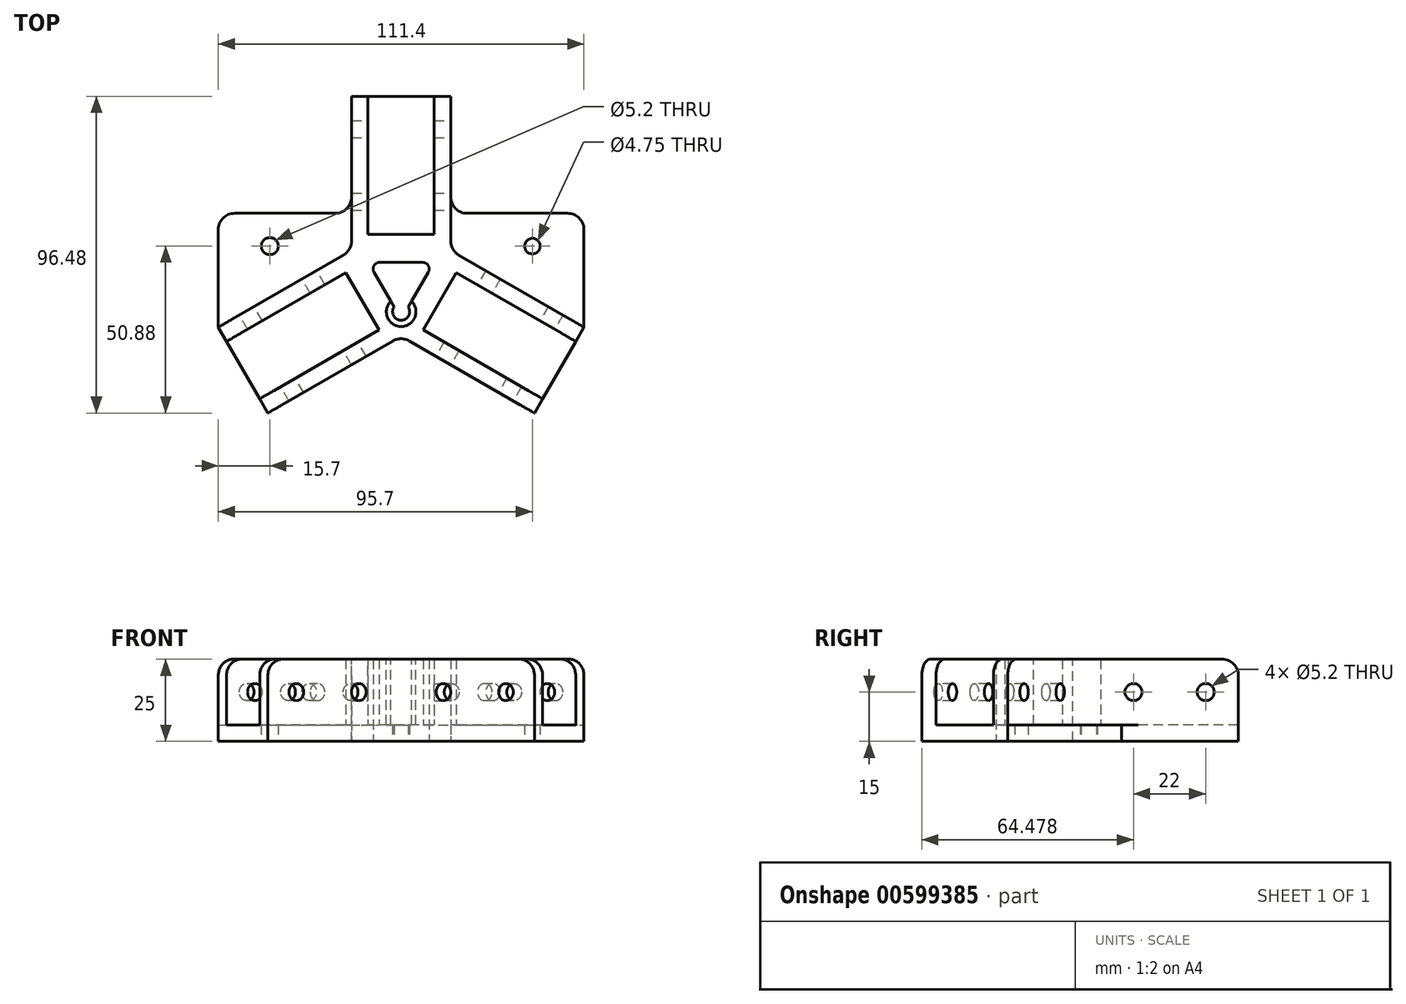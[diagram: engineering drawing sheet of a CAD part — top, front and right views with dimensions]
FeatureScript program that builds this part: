
annotation { "Feature Type Name" : "Feature", "Feature Type Description" : "" }
export const myFeature = defineFeature(function(context is Context, id is Id, definition is map)
    precondition{}
    {
        {
            var Q0;
            Q0=qCreatedBy(makeId("Top.planeOp"),FACE);
            var sketch = newSketch(context, id + "F0", { "sketchPlane" : qUnion([Q0])});
            skLineSegment(sketch, "E0", {"start": v(0, 0) * mm, "end": v(140.3, -81) * mm, "construction": true});
            skLineSegment(sketch, "E1", {"start": v(0, 0) * mm, "end": v(0, 45.49) * mm, "construction": true});
            skLineSegment(sketch, "E2", {"start": v(6.73, -15.55) * mm, "end": v(43.1, -36.55) * mm});
            skLineSegment(sketch, "E3", {"start": v(40.6, -40.88) * mm, "end": v(43.1, -36.55) * mm});
            skLineSegment(sketch, "E4", {"start": v(53.2, -19.05) * mm, "end": v(16.83, 1.95) * mm});
            skLineSegment(sketch, "E5", {"start": v(-0.2, -17.32) * mm, "end": v(40.6, -40.88) * mm});
            skLineSegment(sketch, "E6", {"start": v(55.7, -14.72) * mm, "end": v(14.9, 8.83) * mm});
            skLineSegment(sketch, "E7.trimOffspring", {"start": v(53.2, -19.05) * mm, "end": v(55.7, -14.72) * mm});
            skPoint(sketch, "E8.startSnap0", {"position": v(7.5, -4.33) * mm});
            skPoint(sketch, "E9.orphan", {"position": v(0, -11.66) * mm});
            skLineSegment(sketch, "E10", {"start": v(6.73, -15.55) * mm, "end": v(16.83, 1.95) * mm});
            skLineSegment(sketch, "E11", {"start": v(14.9, 8.83) * mm, "end": v(0, 0) * mm});
            skLineSegment(sketch, "E12", {"start": v(0, 0) * mm, "end": v(-0.2, -17.32) * mm});
            skPoint(sketch, "E13.endSnap0", {"position": v(11.78, -6.8) * mm});
            skLineSegment(sketch, "E14", {"start": v(16.86, 1.81) * mm, "end": v(6.86, -15.5) * mm, "construction": true});
            skLineSegment(sketch, "E15", {"start": v(6.86, -15.5) * mm, "end": v(147.16, -96.5) * mm, "construction": true});
            skLineSegment(sketch, "E16", {"start": v(157.16, -79.19) * mm, "end": v(16.86, 1.81) * mm, "construction": true});
            skLineSegment(sketch, "E17.bottom", {"start": v(-152.4, 152.4) * mm, "end": v(152.4, 152.4) * mm, "construction": true});
            skLineSegment(sketch, "E17.top", {"start": v(-152.4, -152.4) * mm, "end": v(152.4, -152.4) * mm, "construction": true});
            skLineSegment(sketch, "E17.left", {"start": v(-152.4, 152.4) * mm, "end": v(-152.4, -152.4) * mm, "construction": true});
            skLineSegment(sketch, "E17.right", {"start": v(152.4, 152.4) * mm, "end": v(152.4, -152.4) * mm, "construction": true});
            skLineSegment(sketch, "E18.bottom", {"start": v(-250, 230) * mm, "end": v(250, 230) * mm, "construction": true});
            skLineSegment(sketch, "E18.top", {"start": v(-250, -230) * mm, "end": v(250, -230) * mm, "construction": true});
            skLineSegment(sketch, "E18.left", {"start": v(-250, 230) * mm, "end": v(-250, -230) * mm, "construction": true});
            skLineSegment(sketch, "E19.top", {"start": v(-250, 250) * mm, "end": v(250, 250) * mm, "construction": true});
            skLineSegment(sketch, "E19.left", {"start": v(-250, 230) * mm, "end": v(-250, 250) * mm, "construction": true});
            skLineSegment(sketch, "E19.right", {"start": v(250, 230) * mm, "end": v(250, 250) * mm, "construction": true});
            skLineSegment(sketch, "E20.bottom", {"start": v(-250, 250) * mm, "end": v(-270, 250) * mm, "construction": true});
            skLineSegment(sketch, "E20.top", {"start": v(-250, -250) * mm, "end": v(-270, -250) * mm, "construction": true});
            skLineSegment(sketch, "E20.left", {"start": v(-250, 250) * mm, "end": v(-250, -250) * mm, "construction": true});
            skLineSegment(sketch, "E20.right", {"start": v(-270, 250) * mm, "end": v(-270, -250) * mm, "construction": true});
            skLineSegment(sketch, "E21.bottom", {"start": v(250, 250) * mm, "end": v(270, 250) * mm, "construction": true});
            skLineSegment(sketch, "E21.top", {"start": v(250, -250) * mm, "end": v(270, -250) * mm, "construction": true});
            skLineSegment(sketch, "E21.left", {"start": v(250, 250) * mm, "end": v(250, -117.97) * mm, "construction": true});
            skLineSegment(sketch, "E21.right", {"start": v(270, 250) * mm, "end": v(270, -250) * mm, "construction": true});
            skLineSegment(sketch, "E22.bottom", {"start": v(-250, -250) * mm, "end": v(250, -250) * mm, "construction": true});
            skLineSegment(sketch, "E22.left", {"start": v(-250, -250) * mm, "end": v(-250, -230) * mm, "construction": true});
            skLineSegment(sketch, "E22.right", {"start": v(250, -250) * mm, "end": v(250, -230) * mm, "construction": true});
            skLineSegment(sketch, "E23", {"start": v(260, -238.46) * mm, "end": v(260, 217.54) * mm, "construction": true});
            skLineSegment(sketch, "E24.trimOffspring", {"start": v(250, -117.97) * mm, "end": v(250, -250) * mm, "construction": true});
            skPoint(sketch, "E25", {"position": v(152.4, -87.99) * mm});
            skLineSegment(sketch, "E26", {"start": v(147.16, -96.5) * mm, "end": v(157.16, -79.19) * mm, "construction": true});
            skCircle(sketch, "E27", {"center": v(147.4, -85.1) * mm, "radius": 2.65 * mm, "construction": true});
            skSolve(sketch);
        }
        {
            var Q0;
            Q0=qSketchRegion(id+"F0",true);
            extrude(context, id + "F1", {"entities" : qUnion([Q0]), "depth" : 20 * mm});
        }
        {
            var Q0;
            Q0=makeQuery(id+"F8AnNkQhTy7cih4_3.boolean.opBoolean","MERGE",FACE,{"derivedFrom":[makeQuery(id+"F1.opExtrude","SWEPT_FACE",FACE,{"disambiguationData":[OSD([sQuery(id+"F0.wireOp",EDGE,"E5")])]}),makeQuery(id+"F8AnNkQhTy7cih4_3.opExtrude","SWEPT_FACE",FACE,{"disambiguationData":[OSD([sQuery(id+"FXKs39bWKYu9lIt_3.wireOp",EDGE,"d46a372c-ea87-446f-ae03-e79ca4958cda.0")])]})]});
            var sketch = newSketch(context, id + "F2", { "sketchPlane" : qUnion([Q0])});
            skCircle(sketch, "E28", {"center": v(45.6, 10) * mm, "radius": 2.6 * mm});
            skCircle(sketch, "E29", {"center": v(23.6, 10) * mm, "radius": 2.6 * mm});
            skSolve(sketch);
        }
        {
            var Q0;
            Q0=qSketchRegion(id+"F2",true);
            extrude(context, id + "F3", {"entities" : qUnion([Q0]), "operationType" : NewBodyOperationType.REMOVE, "endBound" : BoundingType.THROUGH_ALL, "oppositeDirection" : true, "depth" : 25 * mm});
        }
        {
            var Q0;
            Q0=makeQuery(id+"F1.opExtrude","SWEPT_BODY",BODY,{"disambiguationData":[OSD([sQuery(id+"F0.wireOp",EDGE,"E2"),sQuery(id+"F0.wireOp",EDGE,"E3"),sQuery(id+"F0.wireOp",EDGE,"E4"),sQuery(id+"F0.wireOp",EDGE,"E5"),sQuery(id+"F0.wireOp",EDGE,"E6"),sQuery(id+"F0.wireOp",EDGE,"E7.trimOffspring"),sQuery(id+"F0.wireOp",EDGE,"E10"),sQuery(id+"F0.wireOp",EDGE,"E11"),sQuery(id+"F0.wireOp",EDGE,"E12")])]});
            var Q1;
            Q1=makeQuery(id+"F1.opExtrude","SWEPT_EDGE",EDGE,{"disambiguationData":[OSD([sQuery(id+"F0.wireOp",EDGE,"E11"),sQuery(id+"F0.wireOp",EDGE,"E12")])]});
            circularPattern(context, id + "F4", {"operationType" : NewBodyOperationType.ADD, "entities" : qUnion([Q0]), "axis" : qUnion([Q1]), "angle" : 120 * degree, "instanceCount" : round(3)});
        }
        {
            var Q0;
            {var subQ0=makeQuery(id+"F1.opExtrude","CAP_FACE",FACE,{"disambiguationData":[OSD([sQuery(id+"F0.wireOp",EDGE,"E2"),sQuery(id+"F0.wireOp",EDGE,"E3"),sQuery(id+"F0.wireOp",EDGE,"E4"),sQuery(id+"F0.wireOp",EDGE,"E5"),sQuery(id+"F0.wireOp",EDGE,"E6"),sQuery(id+"F0.wireOp",EDGE,"E7.trimOffspring"),sQuery(id+"F0.wireOp",EDGE,"E10"),sQuery(id+"F0.wireOp",EDGE,"E11"),sQuery(id+"F0.wireOp",EDGE,"E12")])],"isStart":true});Q0=makeQuery(id+"F4.boolean.opBoolean","MERGE",FACE,{"derivedFrom":[subQ0,makeQuery(id+"F4.opPattern","COPY",FACE,{"derivedFrom":subQ0,"instanceName":"1"}),makeQuery(id+"F4.opPattern","COPY",FACE,{"derivedFrom":subQ0,"instanceName":"2"})]});}
            var sketch = newSketch(context, id + "F5", { "sketchPlane" : qUnion([Q0])});
            skLineSegment(sketch, "E30.0", {"start": v(-40.6, 40.88) * mm, "end": v(0, 17.44) * mm});
            skLineSegment(sketch, "E31.0", {"start": v(0, 17.44) * mm, "end": v(40.6, 40.88) * mm});
            skLineSegment(sketch, "E32.0", {"start": v(55.7, 14.72) * mm, "end": v(15.1, -8.72) * mm});
            skLineSegment(sketch, "E33.0", {"start": v(15.1, -8.72) * mm, "end": v(15.1, -55.6) * mm});
            skLineSegment(sketch, "E34.0", {"start": v(-15.1, -55.6) * mm, "end": v(-15.1, -8.72) * mm});
            skLineSegment(sketch, "E35.0", {"start": v(-15.1, -8.72) * mm, "end": v(-55.7, 14.72) * mm});
            skLineSegment(sketch, "E36", {"start": v(-40.6, 40.88) * mm, "end": v(-55.7, 14.72) * mm});
            skLineSegment(sketch, "E37", {"start": v(40.6, 40.88) * mm, "end": v(55.7, 14.72) * mm});
            skLineSegment(sketch, "E38", {"start": v(15.1, -55.6) * mm, "end": v(-15.1, -55.6) * mm});
            skSolve(sketch);
        }
        {
            var Q0;
            Q0=qSketchRegion(id+"F5",true);
            extrude(context, id + "F6", {"entities" : qUnion([Q0]), "operationType" : NewBodyOperationType.ADD, "depth" : 5 * mm});
        }
        {
            var Q0;
            Q0=makeQuery(id+"F6.boolean.opBoolean","MERGE",EDGE,{"derivedFrom":[makeQuery(id+"F4.boolean.opBoolean","INTERSECT",EDGE,{"derivedFrom":[makeQuery(id+"F1.opExtrude","SWEPT_FACE",FACE,{"disambiguationData":[OSD([sQuery(id+"F0.wireOp",EDGE,"E5")])]}),makeQuery(id+"F4.opPattern","COPY",FACE,{"derivedFrom":makeQuery(id+"F1.opExtrude","SWEPT_FACE",FACE,{"disambiguationData":[OSD([sQuery(id+"F0.wireOp",EDGE,"E6")])]}),"instanceName":"1"})]}),makeQuery(id+"F6.opExtrude","SWEPT_EDGE",EDGE,{"disambiguationData":[OSD([sQuery(id+"F5.wireOp",EDGE,"E30.0"),sQuery(id+"F5.wireOp",EDGE,"E31.0")])]})]});
            var Q1;
            Q1=makeQuery(id+"F6.boolean.opBoolean","MERGE",EDGE,{"derivedFrom":[makeQuery(id+"F4.boolean.opBoolean","INTERSECT",EDGE,{"derivedFrom":[makeQuery(id+"F1.opExtrude","SWEPT_FACE",FACE,{"disambiguationData":[OSD([sQuery(id+"F0.wireOp",EDGE,"E6")])]}),makeQuery(id+"F4.opPattern","COPY",FACE,{"derivedFrom":makeQuery(id+"F1.opExtrude","SWEPT_FACE",FACE,{"disambiguationData":[OSD([sQuery(id+"F0.wireOp",EDGE,"E5")])]}),"instanceName":"2"})]}),makeQuery(id+"F6.opExtrude","SWEPT_EDGE",EDGE,{"disambiguationData":[OSD([sQuery(id+"F5.wireOp",EDGE,"E32.0"),sQuery(id+"F5.wireOp",EDGE,"E33.0")])]})]});
            var Q2;
            Q2=makeQuery(id+"F6.boolean.opBoolean","MERGE",EDGE,{"derivedFrom":[makeQuery(id+"F4.boolean.opBoolean","INTERSECT",EDGE,{"derivedFrom":[makeQuery(id+"F4.opPattern","COPY",FACE,{"derivedFrom":makeQuery(id+"F1.opExtrude","SWEPT_FACE",FACE,{"disambiguationData":[OSD([sQuery(id+"F0.wireOp",EDGE,"E5")])]}),"instanceName":"1"}),makeQuery(id+"F4.opPattern","COPY",FACE,{"derivedFrom":makeQuery(id+"F1.opExtrude","SWEPT_FACE",FACE,{"disambiguationData":[OSD([sQuery(id+"F0.wireOp",EDGE,"E6")])]}),"instanceName":"2"})]}),makeQuery(id+"F6.opExtrude","SWEPT_EDGE",EDGE,{"disambiguationData":[OSD([sQuery(id+"F5.wireOp",EDGE,"E34.0"),sQuery(id+"F5.wireOp",EDGE,"E35.0")])]})]});
            fillet(context, id + "F7", {"entities" : qUnion([Q0, Q1, Q2]), "radius" : 5 * mm, "tangentPropagation" : true, "allowEdgeOverflow" : false});
        }
        {
            var Q0;
            {var subQ0=makeQuery(id+"F1.opExtrude","CAP_FACE",FACE,{"disambiguationData":[OSD([sQuery(id+"F0.wireOp",EDGE,"E2"),sQuery(id+"F0.wireOp",EDGE,"E3"),sQuery(id+"F0.wireOp",EDGE,"E4"),sQuery(id+"F0.wireOp",EDGE,"E5"),sQuery(id+"F0.wireOp",EDGE,"E6"),sQuery(id+"F0.wireOp",EDGE,"E7.trimOffspring"),sQuery(id+"F0.wireOp",EDGE,"E10"),sQuery(id+"F0.wireOp",EDGE,"E11"),sQuery(id+"F0.wireOp",EDGE,"E12")])],"isStart":false});Q0=makeQuery(id+"F4.boolean.opBoolean","MERGE",FACE,{"derivedFrom":[subQ0,makeQuery(id+"F4.opPattern","COPY",FACE,{"derivedFrom":subQ0,"instanceName":"1"}),makeQuery(id+"F4.opPattern","COPY",FACE,{"derivedFrom":subQ0,"instanceName":"2"})]});}
            var sketch = newSketch(context, id + "F8", { "sketchPlane" : qUnion([Q0])});
            skLineSegment(sketch, "E39", {"start": v(-10, 5.06) * mm, "end": v(0, -12.26) * mm});
            skLineSegment(sketch, "E40", {"start": v(0, -12.26) * mm, "end": v(10, 5.06) * mm});
            skLineSegment(sketch, "E41", {"start": v(10, 5.06) * mm, "end": v(-10, 5.06) * mm});
            skSolve(sketch);
        }
        {
            var Q0;
            Q0=makeQuery(id+"F6.opExtrude","CAP_FACE",FACE,{"disambiguationData":[OSD([sQuery(id+"F5.wireOp",EDGE,"E30.0"),sQuery(id+"F5.wireOp",EDGE,"E31.0"),sQuery(id+"F5.wireOp",EDGE,"E32.0"),sQuery(id+"F5.wireOp",EDGE,"E33.0"),sQuery(id+"F5.wireOp",EDGE,"E34.0"),sQuery(id+"F5.wireOp",EDGE,"E35.0"),sQuery(id+"F5.wireOp",EDGE,"E36"),sQuery(id+"F5.wireOp",EDGE,"E37"),sQuery(id+"F5.wireOp",EDGE,"E38")])],"isStart":false});
            var sketch = newSketch(context, id + "F9", { "sketchPlane" : qUnion([Q0])});
            skLineSegment(sketch, "E42.top", {"start": v(-55.7, -20) * mm, "end": v(55.7, -20) * mm});
            skLineSegment(sketch, "E42.left", {"start": v(-55.7, 14.72) * mm, "end": v(-55.7, -20) * mm});
            skLineSegment(sketch, "E42.right", {"start": v(55.7, 14.72) * mm, "end": v(55.7, -20) * mm});
            skLineSegment(sketch, "E43", {"start": v(-52.65, 20) * mm, "end": v(-4.44, 20) * mm});
            skLineSegment(sketch, "E44", {"start": v(52.65, 20) * mm, "end": v(55.7, 14.72) * mm});
            skPoint(sketch, "E45.start.orphan", {"position": v(-52.65, 20) * mm});
            skLineSegment(sketch, "E46", {"start": v(-52.65, 20) * mm, "end": v(-55.7, 14.72) * mm});
            skPoint(sketch, "E47.orphan", {"position": v(-55.7, 20) * mm});
            skArc(sketch, "E48.0", {"start": v(2.5, 18.88) * mm, "mid": v(0, 18.2) * mm, "end": v(-2.5, 18.88) * mm});
            skLineSegment(sketch, "E48.1", {"start": v(2.5, 18.88) * mm, "end": v(4.44, 20) * mm});
            skLineSegment(sketch, "E48.2", {"start": v(-4.44, 20) * mm, "end": v(-2.5, 18.88) * mm});
            skPoint(sketch, "E49.orphan", {"position": v(-40.6, 40.88) * mm});
            skPoint(sketch, "E50.orphan", {"position": v(40.6, 40.88) * mm});
            skLineSegment(sketch, "E51.trimOffspring", {"start": v(4.44, 20) * mm, "end": v(52.65, 20) * mm});
            skSolve(sketch);
        }
        {
            var Q0;
            Q0=qSketchRegion(id+"F9",true);
            extrude(context, id + "F10", {"entities" : qUnion([Q0]), "operationType" : NewBodyOperationType.ADD, "oppositeDirection" : true, "depth" : 5 * mm});
        }
        {
            var Q0;
            Q0=qSketchRegion(id+"F8",true);
            extrude(context, id + "F11", {"entities" : qUnion([Q0]), "operationType" : NewBodyOperationType.REMOVE, "endBound" : BoundingType.THROUGH_ALL, "oppositeDirection" : true, "depth" : 25 * mm});
        }
        {
            var Q0;
            Q0=makeQuery(id+"F11.boolean.opBoolean","COPY",EDGE,{"derivedFrom":makeQuery(id+"F11.opExtrude","SWEPT_EDGE",EDGE,{"disambiguationData":[OSD([sQuery(id+"F8.wireOp",EDGE,"E40"),sQuery(id+"F8.wireOp",EDGE,"E41")])]})});
            var Q1;
            Q1=makeQuery(id+"F11.boolean.opBoolean","COPY",EDGE,{"derivedFrom":makeQuery(id+"F11.opExtrude","SWEPT_EDGE",EDGE,{"disambiguationData":[OSD([sQuery(id+"F8.wireOp",EDGE,"E39"),sQuery(id+"F8.wireOp",EDGE,"E41")])]})});
            var Q2;
            Q2=makeQuery(id+"F11.boolean.opBoolean","COPY",EDGE,{"derivedFrom":makeQuery(id+"F11.opExtrude","SWEPT_EDGE",EDGE,{"disambiguationData":[OSD([sQuery(id+"F8.wireOp",EDGE,"E39"),sQuery(id+"F8.wireOp",EDGE,"E40")])]})});
            fillet(context, id + "F12", {"entities" : qUnion([Q0, Q1, Q2]), "radius" : 2 * mm, "tangentPropagation" : true, "allowEdgeOverflow" : false});
        }
        {
            var Q0;
            Q0=makeQuery(id+"F10.boolean.opBoolean","MERGE",FACE,{"derivedFrom":[makeQuery(id+"F6.opExtrude","CAP_FACE",FACE,{"disambiguationData":[OSD([sQuery(id+"F5.wireOp",EDGE,"E30.0"),sQuery(id+"F5.wireOp",EDGE,"E31.0"),sQuery(id+"F5.wireOp",EDGE,"E32.0"),sQuery(id+"F5.wireOp",EDGE,"E33.0"),sQuery(id+"F5.wireOp",EDGE,"E34.0"),sQuery(id+"F5.wireOp",EDGE,"E35.0"),sQuery(id+"F5.wireOp",EDGE,"E36"),sQuery(id+"F5.wireOp",EDGE,"E37"),sQuery(id+"F5.wireOp",EDGE,"E38")])],"isStart":false}),makeQuery(id+"F10.opExtrude","CAP_FACE",FACE,{"disambiguationData":[OSD([sQuery(id+"F9.wireOp",EDGE,"E42.bottom"),sQuery(id+"F9.wireOp",EDGE,"E42.top"),sQuery(id+"F9.wireOp",EDGE,"E42.left"),sQuery(id+"F9.wireOp",EDGE,"E42.right")])],"isStart":true})]});
            var sketch = newSketch(context, id + "F13", { "sketchPlane" : qUnion([Q0])});
            skCircle(sketch, "E52", {"center": v(-40, -10) * mm, "radius": 2.6 * mm});
            skCircle(sketch, "E53", {"center": v(40, -10) * mm, "radius": 2.37 * mm});
            skCircle(sketch, "E54", {"center": v(0, 10) * mm, "radius": 2.6 * mm});
            skSolve(sketch);
        }
        {
            var Q0;
            Q0=qSketchRegion(id+"F13",true);
            extrude(context, id + "F14", {"entities" : qUnion([Q0]), "operationType" : NewBodyOperationType.REMOVE, "endBound" : BoundingType.THROUGH_ALL, "oppositeDirection" : true, "depth" : 25 * mm});
        }
        {
            var Q0;
            Q0=makeQuery(id+"F10.boolean.opBoolean","INTERSECT",EDGE,{"derivedFrom":[makeQuery(id+"F6.boolean.opBoolean","MERGE",FACE,{"derivedFrom":[makeQuery(id+"F4.opPattern","COPY",FACE,{"derivedFrom":makeQuery(id+"F1.opExtrude","SWEPT_FACE",FACE,{"disambiguationData":[OSD([sQuery(id+"F0.wireOp",EDGE,"E6")])]}),"instanceName":"2"}),makeQuery(id+"F6.opExtrude","SWEPT_FACE",FACE,{"disambiguationData":[OSD([sQuery(id+"F5.wireOp",EDGE,"E34.0")])]})]}),makeQuery(id+"F10.opExtrude","SWEPT_FACE",FACE,{"disambiguationData":[OSD([sQuery(id+"F9.wireOp",EDGE,"E42.top")])]})]});
            var Q1;
            Q1=makeQuery(id+"F10.boolean.opBoolean","INTERSECT",EDGE,{"derivedFrom":[makeQuery(id+"F6.boolean.opBoolean","MERGE",FACE,{"derivedFrom":[makeQuery(id+"F4.opPattern","COPY",FACE,{"derivedFrom":makeQuery(id+"F1.opExtrude","SWEPT_FACE",FACE,{"disambiguationData":[OSD([sQuery(id+"F0.wireOp",EDGE,"E5")])]}),"instanceName":"2"}),makeQuery(id+"F6.opExtrude","SWEPT_FACE",FACE,{"disambiguationData":[OSD([sQuery(id+"F5.wireOp",EDGE,"E33.0")])]})]}),makeQuery(id+"F10.opExtrude","SWEPT_FACE",FACE,{"disambiguationData":[OSD([sQuery(id+"F9.wireOp",EDGE,"E42.top")])]})]});
            var Q2;
            Q2=makeQuery(id+"F10.opExtrude","SWEPT_EDGE",EDGE,{"disambiguationData":[OSD([sQuery(id+"F9.wireOp",EDGE,"E42.top"),sQuery(id+"F9.wireOp",EDGE,"E42.right")])]});
            var Q3;
            Q3=makeQuery(id+"F10.opExtrude","SWEPT_EDGE",EDGE,{"disambiguationData":[OSD([sQuery(id+"F9.wireOp",EDGE,"E42.top"),sQuery(id+"F9.wireOp",EDGE,"E42.left")])]});
            var Q4;
            Q4=makeQuery(id+"F4.opPattern","COPY",EDGE,{"derivedFrom":makeQuery(id+"F1.opExtrude","CAP_EDGE",EDGE,{"disambiguationData":[OSD([sQuery(id+"F0.wireOp",EDGE,"E7.trimOffspring")])],"isStart":false}),"instanceName":"2"});
            var Q5;
            Q5=makeQuery(id+"F4.opPattern","COPY",EDGE,{"derivedFrom":makeQuery(id+"F1.opExtrude","CAP_EDGE",EDGE,{"disambiguationData":[OSD([sQuery(id+"F0.wireOp",EDGE,"E3")])],"isStart":false}),"instanceName":"2"});
            var Q6;
            Q6=makeQuery(id+"F4.opPattern","COPY",EDGE,{"derivedFrom":makeQuery(id+"F1.opExtrude","CAP_EDGE",EDGE,{"disambiguationData":[OSD([sQuery(id+"F0.wireOp",EDGE,"E3")])],"isStart":false}),"instanceName":"1"});
            var Q7;
            Q7=makeQuery(id+"F4.opPattern","COPY",EDGE,{"derivedFrom":makeQuery(id+"F1.opExtrude","CAP_EDGE",EDGE,{"disambiguationData":[OSD([sQuery(id+"F0.wireOp",EDGE,"E7.trimOffspring")])],"isStart":false}),"instanceName":"1"});
            var Q8;
            Q8=makeQuery(id+"F1.opExtrude","CAP_EDGE",EDGE,{"disambiguationData":[OSD([sQuery(id+"F0.wireOp",EDGE,"E7.trimOffspring")])],"isStart":false});
            var Q9;
            Q9=makeQuery(id+"F1.opExtrude","CAP_EDGE",EDGE,{"disambiguationData":[OSD([sQuery(id+"F0.wireOp",EDGE,"E3")])],"isStart":false});
            var Q10;
            Q10=makeQuery(id+"F10.opExtrude","SWEPT_EDGE",EDGE,{"disambiguationData":[OSD([sQuery(id+"F9.wireOp",EDGE,"E42.left"),sQuery(id+"F9.wireOp",EDGE,"E43")])]});
            var Q11;
            Q11=makeQuery(id+"F10.opExtrude","SWEPT_EDGE",EDGE,{"disambiguationData":[OSD([sQuery(id+"F9.wireOp",EDGE,"E42.right"),sQuery(id+"F9.wireOp",EDGE,"E43")])]});
            fillet(context, id + "F15", {"entities" : qUnion([Q0, Q1, Q2, Q3, Q4, Q5, Q6, Q7, Q8, Q9, Q10, Q11]), "radius" : 5 * mm, "tangentPropagation" : true, "allowEdgeOverflow" : false});
        }
        {
            var Q0;
            {var subQ0=makeQuery(id+"F1.opExtrude","CAP_FACE",FACE,{"disambiguationData":[OSD([sQuery(id+"F0.wireOp",EDGE,"E2"),sQuery(id+"F0.wireOp",EDGE,"E3"),sQuery(id+"F0.wireOp",EDGE,"E4"),sQuery(id+"F0.wireOp",EDGE,"E5"),sQuery(id+"F0.wireOp",EDGE,"E6"),sQuery(id+"F0.wireOp",EDGE,"E7.trimOffspring"),sQuery(id+"F0.wireOp",EDGE,"E10"),sQuery(id+"F0.wireOp",EDGE,"E11"),sQuery(id+"F0.wireOp",EDGE,"E12")])],"isStart":false});Q0=makeQuery(id+"F4.boolean.opBoolean","MERGE",FACE,{"derivedFrom":[subQ0,makeQuery(id+"F4.opPattern","COPY",FACE,{"derivedFrom":subQ0,"instanceName":"1"}),makeQuery(id+"F4.opPattern","COPY",FACE,{"derivedFrom":subQ0,"instanceName":"2"})]});}
            var sketch = newSketch(context, id + "F16", { "sketchPlane" : qUnion([Q0])});
            skLineSegment(sketch, "E55.0", {"start": v(-2.15, -8.54) * mm, "end": v(-2.15, -8.54) * mm});
            skCircle(sketch, "E56", {"center": v(0, -10) * mm, "radius": 4.5 * mm});
            skSolve(sketch);
        }
        {
            var Q0;
            Q0=qSketchRegion(id+"F16",true);
            extrude(context, id + "F17", {"entities" : qUnion([Q0]), "operationType" : NewBodyOperationType.REMOVE, "oppositeDirection" : true, "depth" : 20 * mm});
        }
    });
